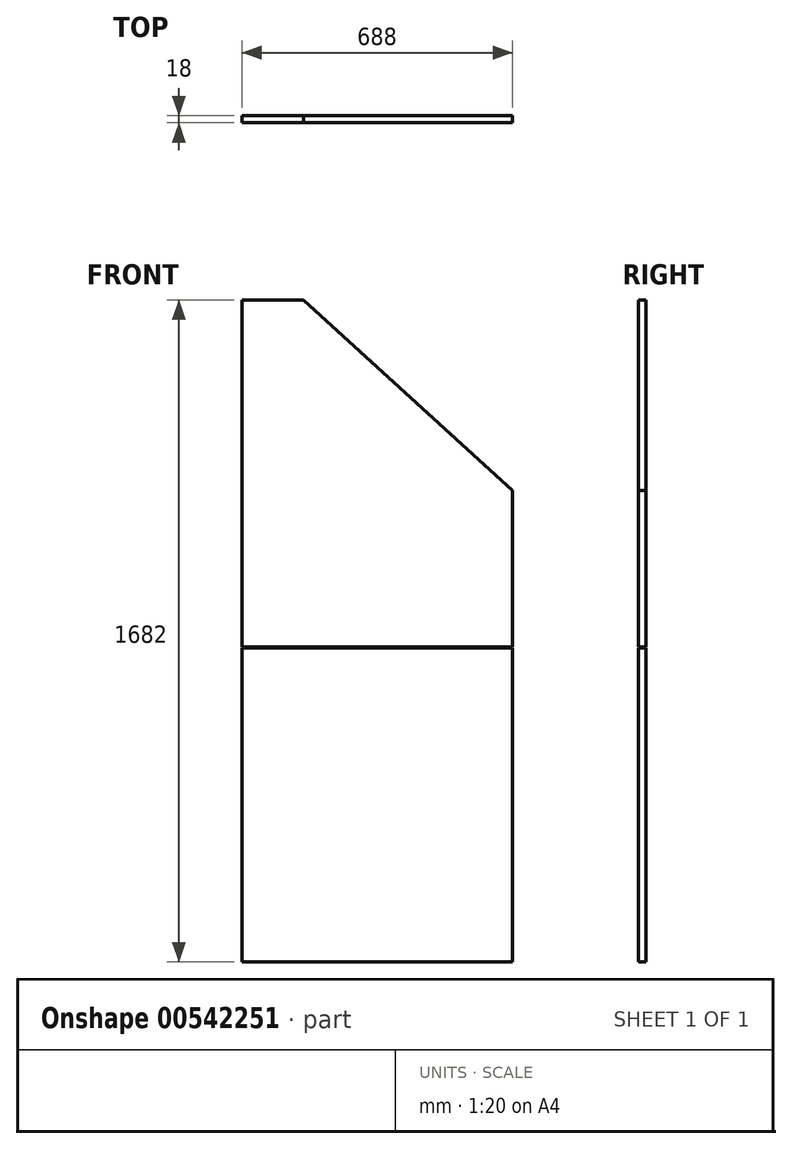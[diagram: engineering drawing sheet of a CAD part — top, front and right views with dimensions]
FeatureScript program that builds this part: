
annotation { "Feature Type Name" : "Feature", "Feature Type Description" : "" }
export const myFeature = defineFeature(function(context is Context, id is Id, definition is map)
    precondition{}
    {
        {
            var Q0;
            Q0=qCreatedBy(makeId("Front.planeOp"),FACE);
            var sketch = newSketch(context, id + "F0", { "sketchPlane" : qUnion([Q0])});
            skLineSegment(sketch, "E0.bottom", {"start": v(0, 0) * mm, "end": v(692, 0) * mm});
            skLineSegment(sketch, "E0.top", {"start": v(0, 1686) * mm, "end": v(159, 1686) * mm});
            skLineSegment(sketch, "E0.left", {"start": v(0, 0) * mm, "end": v(0, 1686) * mm});
            skLineSegment(sketch, "E0.right", {"start": v(692, 0) * mm, "end": v(692, 1200) * mm});
            skLineSegment(sketch, "E1", {"start": v(159, 1686) * mm, "end": v(692, 1200) * mm});
            skSolve(sketch);
        }
        {
            var Q0;
            Q0=qCreatedBy(makeId("Front.planeOp"),FACE);
            var sketch = newSketch(context, id + "F1", { "sketchPlane" : qUnion([Q0])});
            skLineSegment(sketch, "E2.0", {"start": v(158.23, 1684) * mm, "end": v(690, 1199.12) * mm});
            skLineSegment(sketch, "E2.1", {"start": v(2, 1684) * mm, "end": v(158.23, 1684) * mm});
            skLineSegment(sketch, "E2.2", {"start": v(690, 2) * mm, "end": v(690, 1199.12) * mm});
            skLineSegment(sketch, "E2.3", {"start": v(2, 2) * mm, "end": v(690, 2) * mm});
            skLineSegment(sketch, "E2.4", {"start": v(2, 2) * mm, "end": v(2, 1684) * mm});
            skLineSegment(sketch, "E3", {"start": v(2, 800) * mm, "end": v(690, 800) * mm});
            skLineSegment(sketch, "E4", {"start": v(2, 802) * mm, "end": v(690, 802) * mm});
            skSolve(sketch);
        }
        {
            var Q0;
            {var subQ0=sQuery(id+"F1.wireOp",EDGE,"E2.3");Q0=makeQuery(id+"F1.imprint","IMPRINT",FACE,{"disambiguationData":[TD([[makeQuery(id+"F1.imprint","IMPRINT",EDGE,{"derivedFrom":subQ0}),1.0]])]});}
            var Q1;
            {var subQ4=sQuery(id+"F1.wireOp",EDGE,"E2.0");Q1=makeQuery(id+"F1.imprint","IMPRINT",FACE,{"disambiguationData":[TD([[makeQuery(id+"F1.imprint","IMPRINT",EDGE,{"derivedFrom":subQ4}),-1.0]])]});}
            extrude(context, id + "F2", {"entities" : qUnion([Q0, Q1]), "depth" : 18 * mm, "offsetDistance" : 25 * mm});
        }
    });
